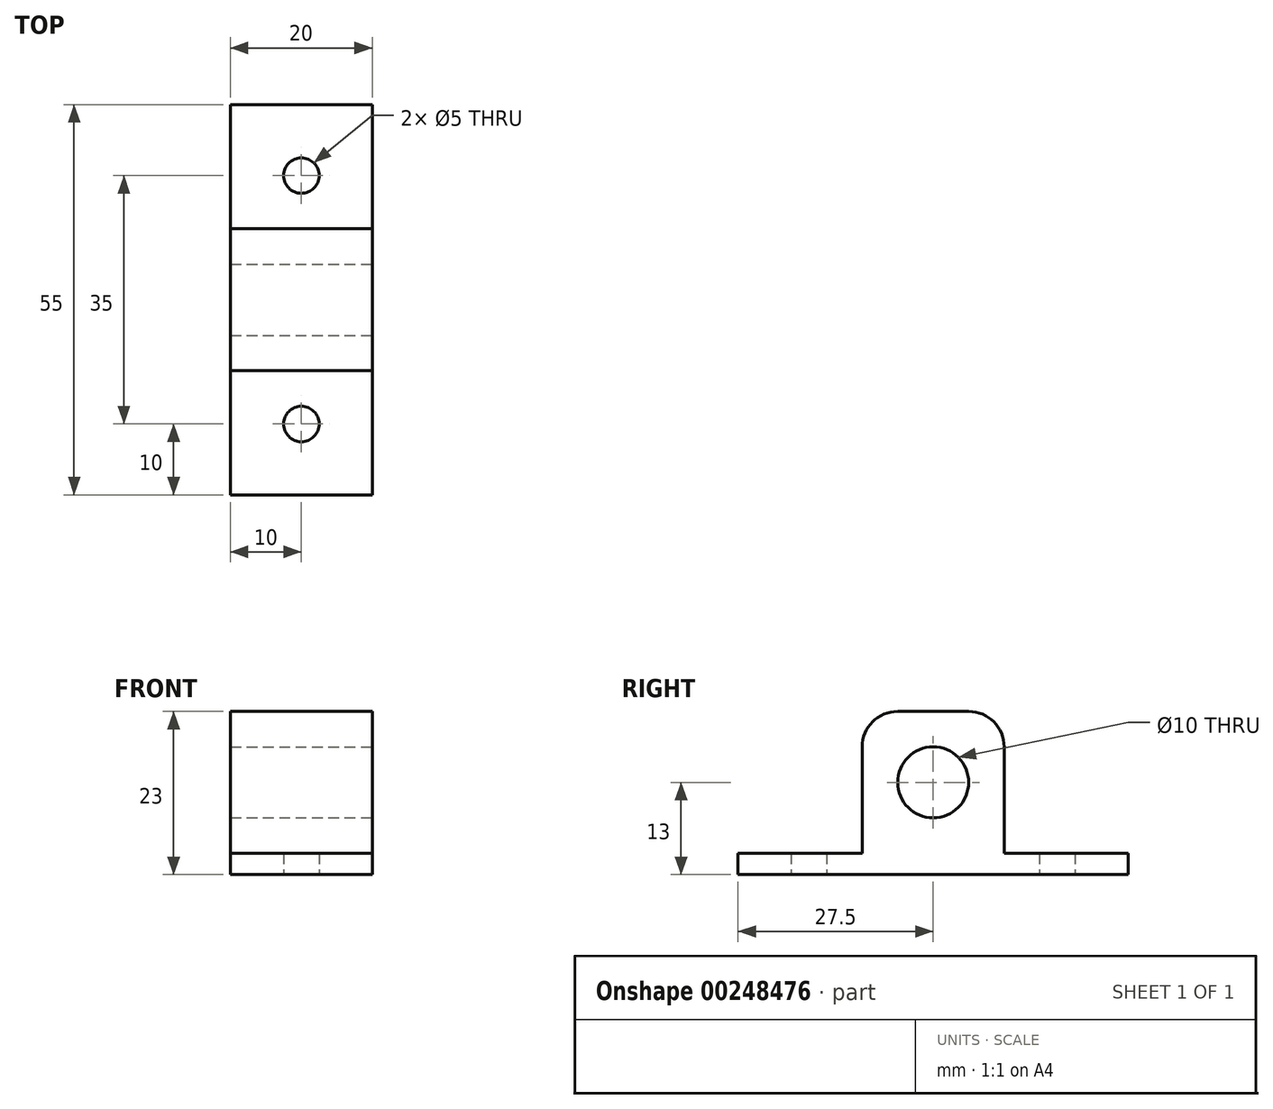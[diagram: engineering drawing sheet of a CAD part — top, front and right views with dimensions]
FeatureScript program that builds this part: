
annotation { "Feature Type Name" : "Feature", "Feature Type Description" : "" }
export const myFeature = defineFeature(function(context is Context, id is Id, definition is map)
    precondition{}
    {
        {
            var Q0;
            Q0=qCreatedBy(makeId("Right.planeOp"),FACE);
            var sketch = newSketch(context, id + "F0", { "sketchPlane" : qUnion([Q0])});
            skLineSegment(sketch, "E0", {"start": v(-27.5, -13) * mm, "end": v(27.5, -13) * mm});
            skLineSegment(sketch, "E1", {"start": v(27.5, -13) * mm, "end": v(27.5, -10) * mm});
            skLineSegment(sketch, "E2", {"start": v(27.5, -10) * mm, "end": v(10, -10) * mm});
            skLineSegment(sketch, "E3", {"start": v(10, -10) * mm, "end": v(10, 10) * mm});
            skLineSegment(sketch, "E4", {"start": v(10, 10) * mm, "end": v(-10, 10) * mm});
            skLineSegment(sketch, "E5", {"start": v(-10, 10) * mm, "end": v(-10, -10) * mm});
            skLineSegment(sketch, "E6", {"start": v(-10, -10) * mm, "end": v(-27.5, -10) * mm});
            skLineSegment(sketch, "E7", {"start": v(-27.5, -10) * mm, "end": v(-27.5, -13) * mm});
            skLineSegment(sketch, "E8", {"start": v(0, 0) * mm, "end": v(-10, -10) * mm, "construction": true});
            skLineSegment(sketch, "E9", {"start": v(0, 0) * mm, "end": v(-10, 10) * mm, "construction": true});
            skLineSegment(sketch, "E10", {"start": v(0, 0) * mm, "end": v(10, 10) * mm, "construction": true});
            skLineSegment(sketch, "E11", {"start": v(10, -10) * mm, "end": v(0, 0) * mm, "construction": true});
            skSolve(sketch);
        }
        {
            var Q0;
            Q0 = qSketchRegion(id + "F0", true);
            extrude(context, id + "F1", {"entities" : qUnion([Q0]), "depth" : 20 * mm});
        }
        {
            var Q0;
            Q0=makeQuery(id+"F1.opExtrude","CAP_FACE",FACE,{"disambiguationData":[OSD([sQuery(id+"F0.wireOp",EDGE,"E0"),sQuery(id+"F0.wireOp",EDGE,"E1"),sQuery(id+"F0.wireOp",EDGE,"E2"),sQuery(id+"F0.wireOp",EDGE,"E3"),sQuery(id+"F0.wireOp",EDGE,"E4"),sQuery(id+"F0.wireOp",EDGE,"E5"),sQuery(id+"F0.wireOp",EDGE,"E6"),sQuery(id+"F0.wireOp",EDGE,"E7")])],"isStart":false});
            var sketch = newSketch(context, id + "F2", { "sketchPlane" : qUnion([Q0])});
            skCircle(sketch, "E12", {"center": v(0, 0) * mm, "radius": 5 * mm});
            skSolve(sketch);
        }
        {
            var Q0;
            Q0 = qSketchRegion(id + "F2", true);
            extrude(context, id + "F3", {"entities" : qUnion([Q0]), "operationType" : NewBodyOperationType.REMOVE, "endBound" : BoundingType.THROUGH_ALL, "oppositeDirection" : true, "depth" : 25 * mm});
        }
        {
            var Q0;
            Q0=makeQuery(id+"F1.opExtrude","SWEPT_EDGE",EDGE,{"disambiguationData":[OSD([sQuery(id+"F0.wireOp",EDGE,"E4"),sQuery(id+"F0.wireOp",EDGE,"E5")])]});
            fillet(context, id + "F4", {"entities" : qUnion([Q0]), "radius" : 5 * mm, "tangentPropagation" : true, "allowEdgeOverflow" : false});
        }
        {
            var Q0;
            Q0=makeQuery(id+"F1.opExtrude","SWEPT_EDGE",EDGE,{"disambiguationData":[OSD([sQuery(id+"F0.wireOp",EDGE,"E3"),sQuery(id+"F0.wireOp",EDGE,"E4")])]});
            fillet(context, id + "F5", {"entities" : qUnion([Q0]), "radius" : 5 * mm, "tangentPropagation" : true, "allowEdgeOverflow" : false});
        }
        {
            var Q0;
            Q0=makeQuery(id+"F1.opExtrude","SWEPT_FACE",FACE,{"disambiguationData":[OSD([sQuery(id+"F0.wireOp",EDGE,"E0")])]});
            var sketch = newSketch(context, id + "F6", { "sketchPlane" : qUnion([Q0])});
            skLineSegment(sketch, "E13", {"start": v(10, 37.7) * mm, "end": v(10, -31.4) * mm, "construction": true});
            skLineSegment(sketch, "E14", {"start": v(0, 10.57) * mm, "end": v(10, 10.57) * mm, "construction": true});
            skLineSegment(sketch, "E15", {"start": v(10, 10.57) * mm, "end": v(20, 10.57) * mm, "construction": true});
            skLineSegment(sketch, "E16", {"start": v(-9.9, 17.5) * mm, "end": v(10, 17.5) * mm, "construction": true});
            skLineSegment(sketch, "E17", {"start": v(10, -17.5) * mm, "end": v(-7.47, -17.5) * mm, "construction": true});
            skCircle(sketch, "E18", {"center": v(10, 17.5) * mm, "radius": 2.5 * mm});
            skCircle(sketch, "E19", {"center": v(10, -17.5) * mm, "radius": 2.5 * mm});
            skSolve(sketch);
        }
        {
            var Q0;
            Q0 = qSketchRegion(id + "F6", true);
            extrude(context, id + "F7", {"entities" : qUnion([Q0]), "operationType" : NewBodyOperationType.REMOVE, "endBound" : BoundingType.THROUGH_ALL, "oppositeDirection" : true, "depth" : 25 * mm});
        }
    });
